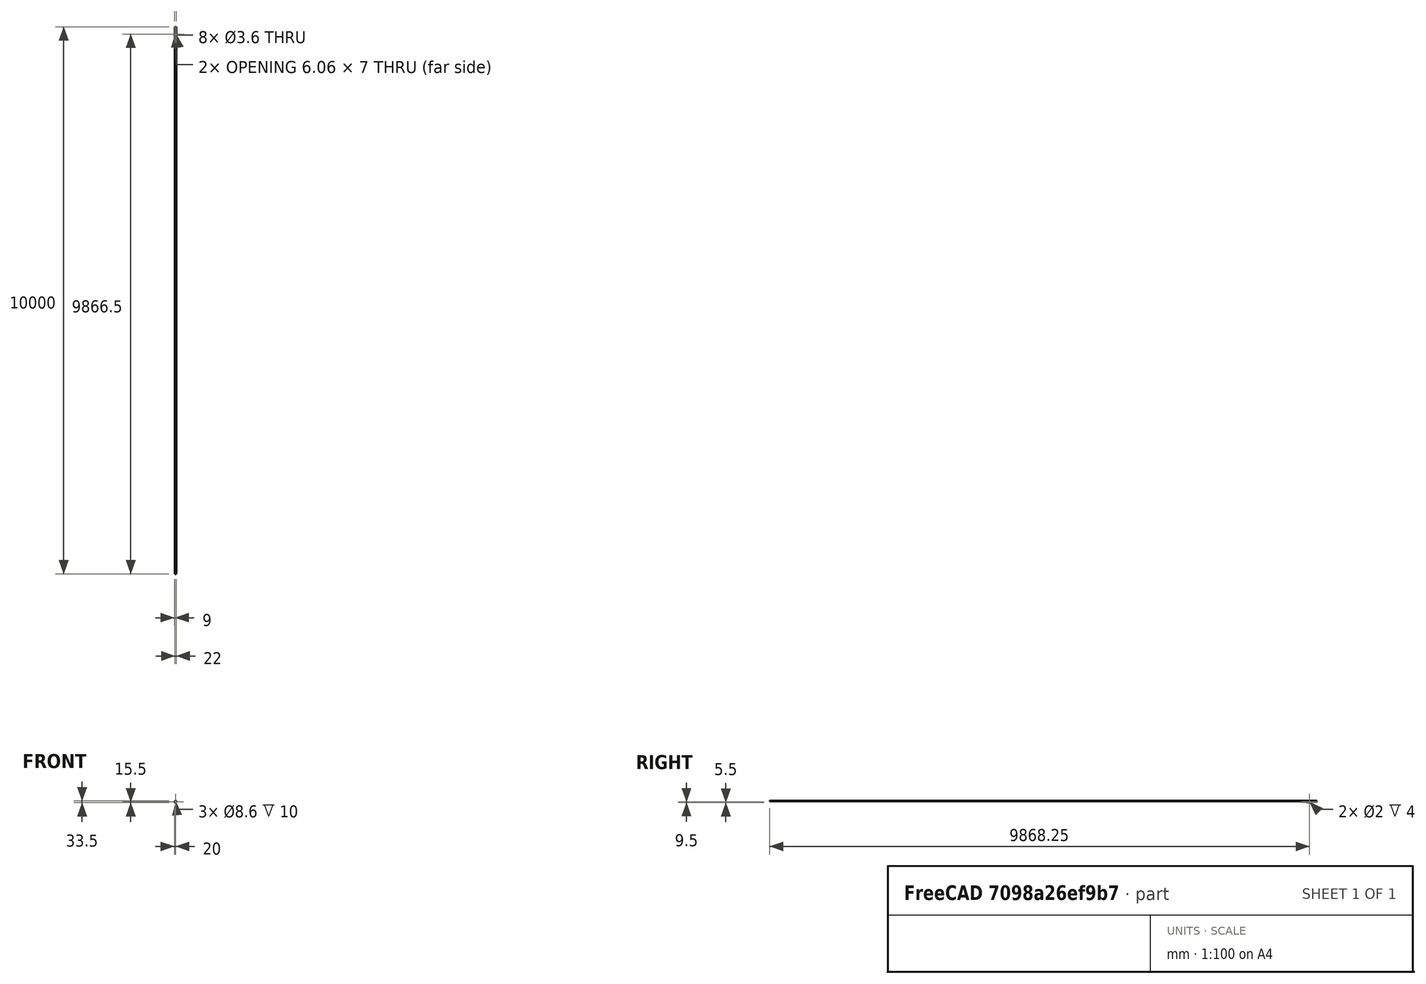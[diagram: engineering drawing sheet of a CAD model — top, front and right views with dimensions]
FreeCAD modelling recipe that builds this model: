
FCSTD DOCUMENT  (FreeCAD 0.15R4671 (Git))
Label: TopRodHolderWithLimitSwitch
License: All rights reserved
LicenseURL: http://en.wikipedia.org/wiki/All_rights_reserved
objects: Sketcher::SketchObject×6, Mesh::Feature×4, PartDesign::Pocket×4, PartDesign::Fillet×3, PartDesign::Pad×2, Part::Feature×1
note: 22 computed .brp shape members not serialized (recipe doc carries the construction recipe); baked Part::Feature solids carry a one-line shape summary decoded from their .brp

FEATURE [Sketcher::SketchObject] Sketch
  Placement = pos=(0,0,0) rot=(1,0,0;3.14159rad)
  sketch-geometry (6):
    g0: LineSegment StartX=51 StartY=69.5 StartZ=0 EndX=21 EndY=69.5 EndZ=0
    g1: LineSegment StartX=21 StartY=69.5 StartZ=0 EndX=21 EndY=58.5 EndZ=0
    g2: LineSegment StartX=21 StartY=58.5 StartZ=0 EndX=51 EndY=58.5 EndZ=0
    g3: LineSegment StartX=51 StartY=58.5 StartZ=0 EndX=51 EndY=69.5 EndZ=0
    g4: Circle CenterX=47 CenterY=64 CenterZ=0 NormalX=0 NormalY=0 NormalZ=1 Radius=1.8
    g5: Circle CenterX=25 CenterY=64 CenterZ=0 NormalX=0 NormalY=0 NormalZ=1 Radius=1.8
  constraints (18):
    c: Coincident(g0,g1)
    c: Coincident(g1,g2)
    c: Coincident(g2,g3)
    c: Coincident(g3,g0)
    c: Horizontal(g0)
    c: Horizontal(g2)
    c: Vertical(g1)
    c: Vertical(g3)
    c: DistanceY(g0,g1) = -11
    c: DistanceX(g0,g0) = 30
    c: DistanceX(g1) = 21
    c: DistanceY(g1) = 58.5
    c: Radius(g4) = 1.8
    c: Radius(g5) = 1.8
    c: DistanceX(g5,g4) = 22
    c: DistanceY(g5,g4) = 0
    c: DistanceX(g5,g1) = -4
    c: DistanceY(g5,g1) = -5.5
FEATURE [Part::Feature] LM8UU_8mm_Linear_Bearing
  Placement = pos=(36,-114.5,-5.5) rot=(0,0,1;1.5708rad)
  shape: bbox 15 x 24 x 15 mm, 34 faces (baked)
FEATURE [Mesh::Feature] _mmRod_x100mm  label="8mmRod_x100mm"
  Placement = pos=(36,-160.5,-5.5) rot=(0,0,1;3.14159rad)
FEATURE [PartDesign::Pad] Pad
  Length = 11.5
  Length2 = 100
  Placement = pos=(0,0,0) rot=(1,0,0;3.14159rad)
  Sketch = -> Sketch
  Type = 0
FEATURE [Sketcher::SketchObject] Sketch001
  Placement = pos=(0,-69.5,0) rot=(0,0.707107,-0.707107;3.14159rad)
  Support = -> Pad [Face1]
  sketch-geometry (6):
    g0: ArcOfCircle CenterX=-36 CenterY=5.5 CenterZ=0 NormalX=0 NormalY=0 NormalZ=1 Radius=6 StartAngle=0 EndAngle=3.14159
    g1: LineSegment StartX=-30 StartY=5.5 StartZ=0 EndX=-20.5 EndY=5.5 EndZ=0
    g2: LineSegment StartX=-20.5 StartY=5.5 StartZ=0 EndX=-20.5 EndY=12.5 EndZ=0
    g3: LineSegment StartX=-20.5 StartY=12.5 StartZ=0 EndX=-51.5 EndY=12.5 EndZ=0
    g4: LineSegment StartX=-51.5 StartY=12.5 StartZ=0 EndX=-51.5 EndY=5.5 EndZ=0
    g5: LineSegment StartX=-51.5 StartY=5.5 StartZ=0 EndX=-42 EndY=5.5 EndZ=0
  constraints (6):
    c: Coincident(g1,g2)
    c: Coincident(g2,g3)
    c: Coincident(g3,g4)
    c: Coincident(g4,g5)
    c: Coincident(g0,g5)
    c: Coincident(g0,g1)
FEATURE [PartDesign::Pocket] Pocket
  Length = 5
  Placement = pos=(0,0,0) rot=(1,0,0;3.14159rad)
  Sketch = -> Sketch001
  Type = 1
FEATURE [Mesh::Feature] HexNutStyle1_M  label="HexNutStyle1_M3"
  Placement = pos=(39.2,-42,-122) rot=(0,0,1;0rad)
FEATURE [Mesh::Feature] HexNutStyle1_M001  label="HexNutStyle1_M004"
  Placement = pos=(61.2,-42,-122) rot=(0,0,1;0rad)
FEATURE [Sketcher::SketchObject] Sketch002
  Placement = pos=(0,0,-5.5) rot=(1,0,0;3.14159rad)
  Support = -> Pocket [Face4]
  sketch-geometry (14):
    g0: LineSegment StartX=25 StartY=67.5 StartZ=0 EndX=21.9689 EndY=65.75 EndZ=0
    g1: LineSegment StartX=21.9689 StartY=65.75 StartZ=0 EndX=21.9689 EndY=62.25 EndZ=0
    g2: LineSegment StartX=21.9689 StartY=62.25 StartZ=0 EndX=25 EndY=60.5 EndZ=0
    g3: LineSegment StartX=25 StartY=60.5 StartZ=0 EndX=28.0311 EndY=62.25 EndZ=0
    g4: LineSegment StartX=28.0311 StartY=62.25 StartZ=0 EndX=28.0311 EndY=65.75 EndZ=0
    g5: LineSegment StartX=28.0311 StartY=65.75 StartZ=0 EndX=25 EndY=67.5 EndZ=0
    g6: Circle [constr] CenterX=25 CenterY=64 CenterZ=0 NormalX=0 NormalY=0 NormalZ=1 Radius=3.5
    g7: LineSegment StartX=47 StartY=67.5 StartZ=0 EndX=43.9689 EndY=65.75 EndZ=0
    g8: LineSegment StartX=43.9689 StartY=65.75 StartZ=0 EndX=43.9689 EndY=62.25 EndZ=0
    g9: LineSegment StartX=43.9689 StartY=62.25 StartZ=0 EndX=47 EndY=60.5 EndZ=0
    g10: LineSegment StartX=47 StartY=60.5 StartZ=0 EndX=50.0311 EndY=62.25 EndZ=0
    g11: LineSegment StartX=50.0311 StartY=62.25 StartZ=0 EndX=50.0311 EndY=65.75 EndZ=0
    g12: LineSegment StartX=50.0311 StartY=65.75 StartZ=0 EndX=47 EndY=67.5 EndZ=0
    g13: Circle [constr] CenterX=47 CenterY=64 CenterZ=0 NormalX=0 NormalY=0 NormalZ=1 Radius=3.5
  constraints (26):
    c: Coincident(g0,g1)
    c: Coincident(g1,g2)
    c: Coincident(g2,g3)
    c: Coincident(g3,g4)
    c: Coincident(g4,g5)
    c: Coincident(g5,g0)
    c: Equal(g0, g1-g5) x5
    c: PointOnObject(g0,g6)
    c: PointOnObject(g1,g6)
    c: PointOnObject(g2,g6)
    c: PointOnObject(g3,g6)
    c: PointOnObject(g4,g6)
    c: PointOnObject(g5,g6)
    c: Coincident(g7,g8)
    c: Coincident(g8,g9)
    c: Coincident(g9,g10)
    c: Coincident(g10,g11)
    c: Coincident(g11,g12)
    c: Coincident(g12,g7)
    c: Equal(g7, g8-g12) x5
    c: PointOnObject(g7,g13)
    c: PointOnObject(g8,g13)
    c: PointOnObject(g9,g13)
    c: PointOnObject(g10,g13)
    c: PointOnObject(g11,g13)
    c: PointOnObject(g12,g13)
FEATURE [PartDesign::Pocket] Pocket001
  Length = 4
  Placement = pos=(0,0,0) rot=(1,0,0;3.14159rad)
  Sketch = -> Sketch002
  Type = 0
FEATURE [Sketcher::SketchObject] Sketch003
  Placement = pos=(0,-69.5,0) rot=(0,0.707107,-0.707107;3.14159rad)
  Support = -> Pocket001 [Face1]
  sketch-geometry (1):
    g0: Circle CenterX=-36 CenterY=5.5 CenterZ=0 NormalX=0 NormalY=0 NormalZ=1 Radius=4.3
  constraints (1):
    c: Radius(g0) = 4.3
FEATURE [PartDesign::Pocket] Pocket002
  Length = 10
  Placement = pos=(0,0,0) rot=(1,0,0;3.14159rad)
  Sketch = -> Sketch003
  Type = 0
FEATURE [PartDesign::Fillet] Fillet
  Base = -> Pocket002 [Edge18,Edge26]
  Placement = pos=(0,0,0) rot=(1,0,0;3.14159rad)
  Radius = 2
FEATURE [Mesh::Feature] MicroSwitch
  Placement = pos=(9.4,-65,-11) rot=(0.707107,0,0.707107;3.14159rad)
FEATURE [Sketcher::SketchObject] Sketch004
  Placement = pos=(21,0,0) rot=(0.57735,0.57735,-0.57735;4.18879rad)
  Support = -> Fillet [Face8]
  sketch-geometry (4):
    g0: LineSegment StartX=-58.5 StartY=0 StartZ=0 EndX=-69.5 EndY=0 EndZ=0
    g1: LineSegment StartX=-69.5 StartY=0 StartZ=0 EndX=-69.5 EndY=21 EndZ=0
    g2: LineSegment StartX=-69.5 StartY=21 StartZ=0 EndX=-58.5 EndY=21 EndZ=0
    g3: LineSegment StartX=-58.5 StartY=21 StartZ=0 EndX=-58.5 EndY=0 EndZ=0
  constraints (8):
    c: Coincident(g0,g1)
    c: Coincident(g1,g2)
    c: Coincident(g2,g3)
    c: Coincident(g3,g0)
    c: Horizontal(g0)
    c: Horizontal(g2)
    c: Vertical(g1)
    c: Vertical(g3)
FEATURE [PartDesign::Pad] Pad001
  Length = 5
  Length2 = 100
  Placement = pos=(0,0,0) rot=(1,0,0;3.14159rad)
  Sketch = -> Sketch004
  Type = 0
FEATURE [Sketcher::SketchObject] Sketch005
  Placement = pos=(16,0,0) rot=(0.57735,0.57735,-0.57735;4.18879rad)
  Support = -> Pad001 [Face3]
  sketch-geometry (2):
    g0: Circle CenterX=-62.25 CenterY=15.5 CenterZ=0 NormalX=0 NormalY=0 NormalZ=1 Radius=1
    g1: Circle CenterX=-62.25 CenterY=6 CenterZ=0 NormalX=0 NormalY=0 NormalZ=1 Radius=1
  constraints (2):
    c: Radius(g0) = 1
    c: Equal(g0,g1)
FEATURE [PartDesign::Pocket] Pocket003
  Length = 4
  Placement = pos=(0,0,0) rot=(1,0,0;3.14159rad)
  Sketch = -> Sketch005
  Type = 0
FEATURE [PartDesign::Fillet] Fillet001
  Base = -> Pocket003 [Edge28,Edge7]
  Placement = pos=(0,0,0) rot=(1,0,0;3.14159rad)
  Radius = 2
FEATURE [PartDesign::Fillet] Fillet002  label="TopRodHolderWithLimitSwitch"
  Base = -> Fillet001 [Edge41,Edge7]
  Placement = pos=(0,0,0) rot=(1,0,0;3.14159rad)
  Radius = 2
